# Revit family: 0030313
name_source: partatom
category: Lighting Fixtures
revit_build: Autodesk Revit 2016 (Build: 20150220_1215(x64)
units: mm (PartAtom-declared; Revit-internal decimal feet)

## family parameters
Cut with Voids When Loaded = No
Host = Face
Light Source = Yes
OmniClass Number = 23.80.70.00
OmniClass Title = Lighting
Part Type = Normal
Room Calculation Point = No
Round Connector Dimension = Use Diameter
Shared = No

## types (1)
- 0030313 Insaver Slim S UGR19 IP44 150 1025lm 840
    Apparent Load = 9 VA
    Assembly Code = D5020200
    AssetType = Fixed
    ClassificationName = Uniclass2015
    ClassificationValue = EF_70_80
    Color Filter = 16777215
    Cost = 0 $
    Default Elevation = 1219 mm
    DiameterRecess_SYL = 137 mm  [stored 0.449475 ft]
    DiameterTop_SYL = 98 mm  [stored 0.321522 ft]
    Diameter_SYL = 165 mm  [stored 0.541339 ft]
    Dimming Lamp Color Temperature Shift = <None>
    DocumentationLiterature = http://www.sylvania-lighting.com
    DurationUnit = hours
    ElectricShockClassification = Class II
    Emit Shape Visible in Rendering = No
    Emit from Rectangle Length = 125 mm  [stored 0.410105 ft]
    Emit from Rectangle Width = 125 mm  [stored 0.410105 ft]
    ExpectedLife = 50000
    HeightBezel_SYL = 3 mm  [stored 0.00984252 ft]
    Height_SYL = 61 mm  [stored 0.200131 ft]
    IfcExportAs = IfcLightFixtureType
    IfcExportType = IfcLightFixtureType
    ImpactProtectionIndex = IK07
    IngressProtection = IP40/20
    InputNominalFrequency = 50/60 Hz
    InputVoltage = AC 220-240 V
    Keynote = 16500
    Lamp = LED
    LampColourRenderingIndex = 80
    LampColourTemperature = 4000 K
    LampMacAdamStep = 5
    LampNominalLuminous = 1025 lm
    LampsType = LED
    LuminousEfficacy = 114 lm/W
    Manufacturer = Feilo Sylvania
    ManufacturerName = Feilo Sylvania
    Material = aluminium housing, na diffuser
    Material_1_FEILO = Trim-Sylvania-STARTDownlight-White
    Material_2_FEILO = Diffuser-Sylvania-STARTDownlight
    Material_3_FEILO = Top-Sylvania-STARTDownlight
    Material_4_FEILO = Reflector-Sylvania-STARTDownlight
    Model = Insaver Slim Square UGR19 IP44 150 1025lm 840
    ModelNumber = 0030313
    ModelReference = Insaver Slim Square UGR19 IP44 150 1025lm 840
    Name = Insaver Slim Square UGR19 IP44 150 1025lm 840
    NominalDepth = 167 mm
    NominalHeight = 50 mm
    NominalLength = 167 mm
    Photometric Web File = 0030313.ies
    PowerConsumption = 9 W
    PowerFactor = 0.9
    SizeSq1_SYL = Yes
    Tilt Angle = -90.00°
    Type Image = <None>
    TypeName = Insaver Slim Square UGR19 IP44 150 1025lm 840
    URL = http://www.sylvania-lighting.com
    Voltage = 230 V
    Weight = 6.72 kg
    WidthDiffuser_SYL = 125 mm  [stored 0.410105 ft]
    WidthLED_SYL = 30 mm  [stored 0.0984252 ft]

note: [stored X ft] marks values corroborated as IEEE doubles in the binary element streams (Revit-internal decimal feet)

## geometry (parser evidence)
native form markers: Sweep x3
no freeform markers — native parametric forms only
